# Revit family: TD92_VER340_REB016_RVT20_R00
name_source: partatom
category: Mobiliário
units: mm (PartAtom-declared; Revit-internal decimal feet)

## family parameters
Com base no plano de trabalho = Não
Compartilhado = Não
Corte com vazios quando carregada = Não
Número OmniClass = 23.40.20.00
Ponto de cálculo do ambiente = Não
Sempre na vertical = Sim
Título OmniClass = General Furniture and Specialties

## types (1)
- TD92_VER340_REB016_RVT20_R00
    Descrição = Mesa Tramontina Infantil Versa em Polipropileno leva mais criatividade e diversão para a hora da brincadeira. Com seu design moderno, ela possui um fundo falso que recria a sensação de compartimento secreto, onde as crianças podem guardar e esconder seus brinquedos quando quiserem. Produzida em polipropileno e tecnologia de ponta, são submetidas a rigorosos testes, garantindo alta qualidade. A mesa perfeita para o dia a dia das crianças!
    Elevação padrão = 0  [stored 0 ft]
    Fabricante = Tramontina Delta S/A
    Modelo = Mesa Infantil Tramontina Versa em Polipropileno Rosa e Branco
    Nota-chave = 92340016
    URL = https://www.tramontinastore.com

note: [stored X ft] marks values corroborated as IEEE doubles in the binary element streams (Revit-internal decimal feet)
